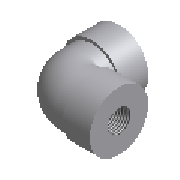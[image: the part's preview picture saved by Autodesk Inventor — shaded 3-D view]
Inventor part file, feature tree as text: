
AUTODESK INVENTOR PART (.ipt)
format: ipt  version: 2025 (Build 290162000, 162)  size: 264,192 bytes
history: native  units: mm (DEFAULTED — no unit token found)
features: other x6, revolve x4
ambient origin geometry x8: Origin, YZ Plane, XZ Plane, XY Plane, X Axis, Y Axis, Z Axis, Center Point
bodies: Solid1 (feature_tree)
feature tree (10):
  revolve  "Revolve1"  [1 undecoded]
  revolve  "Revolve2"  [1 undecoded]
  revolve  "Revolve3"  [1 undecoded]
  revolve  "Revolve4"  [1 undecoded]
  other  "Work Axis1"
  other  "Work Point1"
  other  "Work Point2"
  other  "Work Axis2"
  other  "Work Point3"
  other  "Work Point4"
note: 4 required parameter values undecoded (feature->parameter linkage not recoverable at this tier; creation-order binding heuristic only, values carry confidence <= 0.55)
